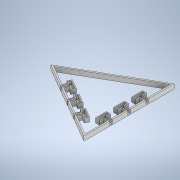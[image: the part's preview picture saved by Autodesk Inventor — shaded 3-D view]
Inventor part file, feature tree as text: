
AUTODESK INVENTOR PART (.ipt)
format: ipt  version: 2022.3 (Build 263350000, 350)  size: 582,656 bytes
history: native  units: mm
features: extrude x7, thicken_offset x6, sketch x5, projected_geometry x2, hole x1
ambient origin geometry x8: Origin, YZ Plane, XZ Plane, XY Plane, X Axis, Y Axis, Z Axis, Center Point
bodies: Solid1 (feature_tree)
feature tree (21):
  sketch  "Sketch1"  dims[d1=200.0mm d2=35.0mm]
  extrude  "Extrusion1"  Depth=35.0mm
  extrude  "Extrusion2"  Depth=5.0mm
  extrude  "Extrusion3"  Depth=40.0mm
  extrude  "Extrusion4"  Depth=10.0mm TaperAngle=0.0deg
  sketch  "Sketch3"  dims[d5=20.0mm d6=30.0mm d8=40.0mm d9=30.0mm d11=40.0mm]
  extrude  "Extrusion6"  Depth=22.0mm
  extrude  "Extrusion7"  Depth=3.0mm
  hole  "Hole1"  [1 undecoded]
  thicken_offset  "Thicken1"
  thicken_offset  "Thicken2"
  thicken_offset  "Thicken3"
  thicken_offset  "Thicken4"
  thicken_offset  "Thicken5"
  thicken_offset  "Thicken6"
  extrude  "Extrusion8"  Depth=40.0mm
  sketch  "Sketch2"  dims[d3=5.0mm d4=5.0mm]
  projected_geometry  "Projected Loop1"
  sketch  "Sketch4"  dims[d14=10.0mm d15=0.0mm d16=10.0mm d17=0.0mm]
  sketch  "Sketch5"  dims[d18=2.2mm d19=0.0mm d20=22.0mm d21=3.0mm d22=1.5mm d23=0.0mm d24=15.0mm d25=120.0deg d26=10.0mm d27=5.0mm d28=20.0mm d29=90.0deg d30=5.0mm d31=2.5mm d32=5.0mm d33=20.0mm d35=120.0deg d37=30.0mm d39=40.0mm d40=30.0mm d42=40.0mm d45=30.0mm d47=40.0mm d48=30.0mm d50=40.0mm d55=7.8mm d56=0.0mm d57=10.0mm d58=0.0mm d59=40.0mm d60=2.2mm d61=6.0mm d62=3.1mm d63=4.1mm d64=90.0deg d65=2.2mm d66=0.0mm d67=0.1mm d68=0.05mm d69=0.1mm d70=0.05mm d71=0.1mm d72=0.05mm d73=0.1mm d74=0.05mm d75=0.1mm d76=0.05mm d77=0.1mm d78=0.05mm d79=3.0mm d80=38.2mm d81=24.2mm d82=20.0mm d84=40.0mm d85=20.0mm d87=40.0mm d90=20.0mm d92=240.0deg d94=0.0mm d95=0.0mm d96=9.9mm d97=7.5mm d98=9.9mm d99=7.5mm d100=20.0mm d102=40.0mm d103=20.0mm d105=40.0mm d108=20.0mm d110=240.0deg]
  projected_geometry  "Projected Loop2"
note: 1 required parameter value undecoded (feature->parameter linkage not recoverable at this tier; creation-order binding heuristic only, values carry confidence <= 0.55)
